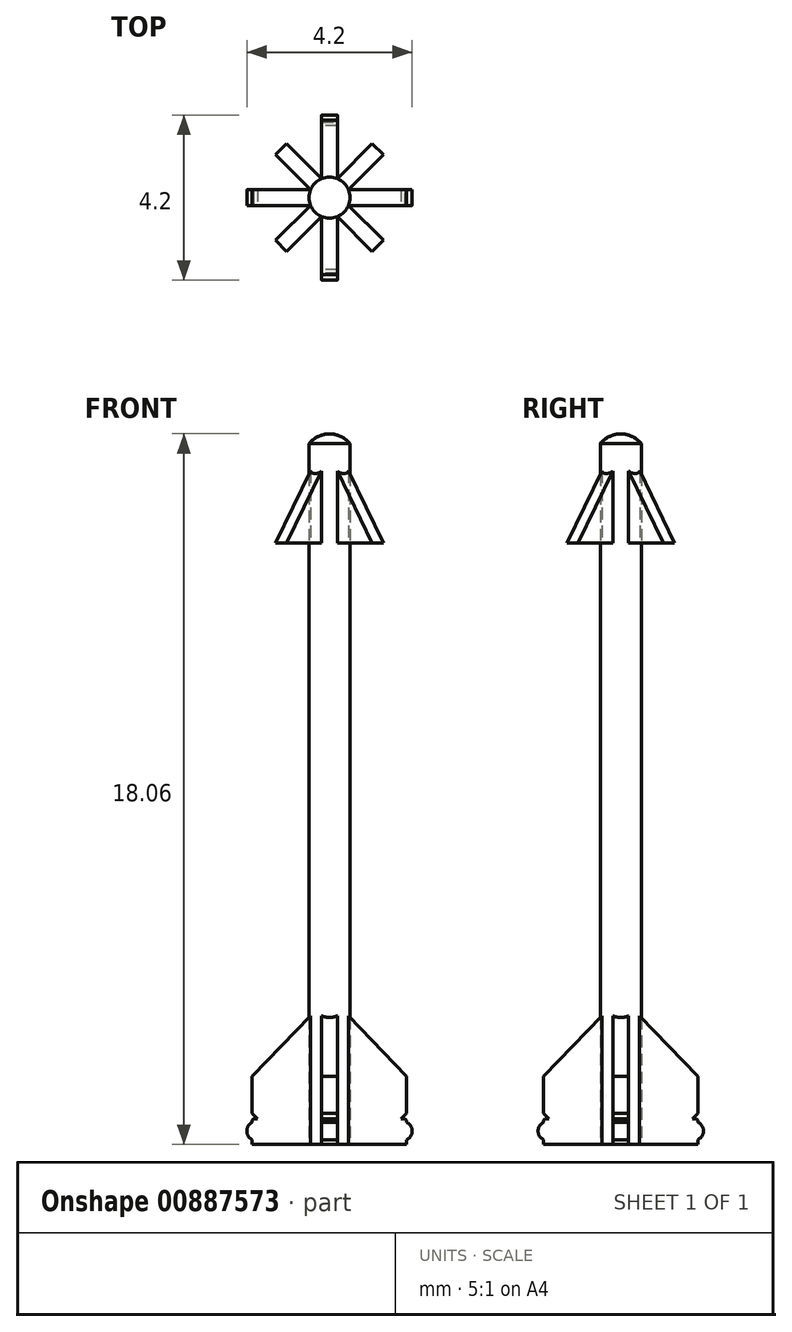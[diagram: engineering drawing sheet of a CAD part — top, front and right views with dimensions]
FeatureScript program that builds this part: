
annotation { "Feature Type Name" : "Feature", "Feature Type Description" : "" }
export const myFeature = defineFeature(function(context is Context, id is Id, definition is map)
    precondition{}
    {
        {
            var Q0;
            Q0=qCreatedBy(makeId("Front.planeOp"),FACE);
            var sketch = newSketch(context, id + "F0", { "sketchPlane" : qUnion([Q0])});
            skLineSegment(sketch, "E0", {"start": v(0, 0) * mm, "end": v(0, 18.06) * mm});
            skLineSegment(sketch, "E1", {"start": v(0.52, 17.8) * mm, "end": v(0.52, 0) * mm});
            skLineSegment(sketch, "E2", {"start": v(0.52, 0) * mm, "end": v(0, 0) * mm});
            skArc(sketch, "E3", {"start": v(0.52, 17.8) * mm, "mid": v(0.29, 17.99) * mm, "end": v(0, 18.06) * mm});
            skLineSegment(sketch, "E4", {"start": v(0, 18.06) * mm, "end": v(1.85, 18.06) * mm, "construction": true});
            skSolve(sketch);
        }
        {
            var Q0;
            Q0 = qSketchRegion(id + "F0", true);
            var Q1;
            Q1=sQuery(id+"F0.wireOp",EDGE,"E0");
            revolve(context, id + "F1", {"surfaceOperationType" : NewSurfaceOperationType.NEW, "entities" : qUnion([Q0]), "axis" : qUnion([Q1]), "revolveType" : RevolveType.FULL});
        }
        {
            var Q0;
            Q0=qCreatedBy(makeId("Front.planeOp"),FACE);
            var sketch = newSketch(context, id + "F2", { "sketchPlane" : qUnion([Q0])});
            skLineSegment(sketch, "E5", {"start": v(0.33, 3.43) * mm, "end": v(-0.33, 3.43) * mm});
            skLineSegment(sketch, "E6", {"start": v(-1.96, 1.74) * mm, "end": v(-0.33, 3.43) * mm});
            skLineSegment(sketch, "E7", {"start": v(-1.96, 1.74) * mm, "end": v(-1.96, 0.8) * mm});
            skLineSegment(sketch, "E8", {"start": v(-1.96, 0) * mm, "end": v(1.96, 0) * mm});
            skLineSegment(sketch, "E9", {"start": v(1.96, 0.8) * mm, "end": v(1.96, 1.74) * mm});
            skLineSegment(sketch, "E10", {"start": v(0.33, 3.43) * mm, "end": v(1.96, 1.74) * mm});
            skLineSegment(sketch, "E11", {"start": v(0, 0) * mm, "end": v(0, 3.43) * mm, "construction": true});
            skLineSegment(sketch, "E12", {"start": v(-0.52, 0) * mm, "end": v(-0.52, 4.16) * mm, "construction": true});
            skLineSegment(sketch, "E13.0", {"start": v(0.52, 17.8) * mm, "end": v(-0.52, 17.8) * mm});
            skPoint(sketch, "E14", {"position": v(-0.52, 3.23) * mm});
            skLineSegment(sketch, "E15", {"start": v(-1.96, 0) * mm, "end": v(-1.96, 0.12) * mm});
            skLineSegment(sketch, "E16", {"start": v(1.96, 0) * mm, "end": v(1.96, 0.12) * mm});
            skLineSegment(sketch, "E17", {"start": v(1.96, 0.8) * mm, "end": v(1.82, 0.66) * mm});
            skLineSegment(sketch, "E18", {"start": v(1.96, 0.61) * mm, "end": v(1.96, 0.56) * mm});
            skLineSegment(sketch, "E19", {"start": v(-1.96, 0.8) * mm, "end": v(-1.82, 0.66) * mm});
            skLineSegment(sketch, "E20", {"start": v(-1.96, 0.62) * mm, "end": v(-1.96, 0.56) * mm});
            skArc(sketch, "E21", {"start": v(-1.96, 0.56) * mm, "mid": v(-2.1, 0.34) * mm, "end": v(-1.96, 0.13) * mm});
            skArc(sketch, "E22", {"start": v(1.96, 0.13) * mm, "mid": v(2.1, 0.34) * mm, "end": v(1.96, 0.56) * mm});
            skLineSegment(sketch, "E23", {"start": v(-1.96, 0.62) * mm, "end": v(-1.92, 0.66) * mm});
            skLineSegment(sketch, "E24", {"start": v(-1.92, 0.66) * mm, "end": v(-1.82, 0.66) * mm});
            skLineSegment(sketch, "E25", {"start": v(1.96, 0.61) * mm, "end": v(1.93, 0.66) * mm});
            skLineSegment(sketch, "E26", {"start": v(1.93, 0.66) * mm, "end": v(1.82, 0.66) * mm});
            skSolve(sketch);
        }
        {
            var Q0;
            Q0 = qSketchRegion(id + "F2", true);
            extrude(context, id + "F3", {"entities" : qUnion([Q0]), "operationType" : NewBodyOperationType.ADD, "depth" : .4 * mm, "offsetDistance" : 25 * mm, "symmetric" : true});
        }
        {
            var Q0;
            Q0=qCreatedBy(makeId("Front.planeOp"),FACE);
            var Q1;
            Q1=qCreatedBy(makeId("Right.planeOp"),FACE);
            cPlane(context, id + "F4", {"entities" : qUnion([Q0, Q1]), "cplaneType" : CPlaneType.MID_PLANE, "offset" : 25 * mm, "width" : 150 * mm, "height" : 150 * mm});
        }
        {
            var Q0;
            Q0=qCreatedBy(id+"F4.planeOp",FACE);
            var sketch = newSketch(context, id + "F5", { "sketchPlane" : qUnion([Q0])});
            skLineSegment(sketch, "E27", {"start": v(-0.06, 17.73) * mm, "end": v(-1.74, 15.28) * mm});
            skLineSegment(sketch, "E28", {"start": v(-1.74, 15.28) * mm, "end": v(1.74, 15.28) * mm});
            skLineSegment(sketch, "E29", {"start": v(1.74, 15.28) * mm, "end": v(0.06, 17.73) * mm});
            skLineSegment(sketch, "E30", {"start": v(0.06, 17.73) * mm, "end": v(-0.06, 17.73) * mm});
            skLineSegment(sketch, "E31.0", {"start": v(0.52, 17.8) * mm, "end": v(-0.52, 17.8) * mm});
            skLineSegment(sketch, "E32", {"start": v(-0.52, 17.8) * mm, "end": v(-0.52, 15.86) * mm, "construction": true});
            skPoint(sketch, "E33", {"position": v(-0.52, 17.05) * mm});
            skLineSegment(sketch, "E34", {"start": v(0, 0) * mm, "end": v(0, 15.28) * mm, "construction": true});
            skPoint(sketch, "E34.endSnap0", {"position": v(0, 15.28) * mm});
            skSolve(sketch);
        }
        {
            var Q0;
            Q0 = qSketchRegion(id + "F5", true);
            extrude(context, id + "F6", {"entities" : qUnion([Q0]), "operationType" : NewBodyOperationType.ADD, "depth" : .4 * mm, "offsetDistance" : 25 * mm, "symmetric" : true});
        }
        {
            var Q0;
            Q0=makeQuery(id+"F1.opRevolve","SWEPT_BODY",BODY,{"disambiguationData":[OSD([sQuery(id+"F0.wireOp",EDGE,"E0"),sQuery(id+"F0.wireOp",EDGE,"E1"),sQuery(id+"F0.wireOp",EDGE,"E2"),sQuery(id+"F0.wireOp",EDGE,"E3")])]});
            var Q1;
            Q1=makeQuery(id+"F1.opRevolve","SWEPT_FACE",FACE,{"disambiguationData":[OSD([sQuery(id+"F0.wireOp",EDGE,"E1")])]});
            circularPattern(context, id + "F7", {"entities" : qUnion([Q0]), "axis" : qUnion([Q1]), "angle" : 360 * degree, "instanceCount" : 4, "equalSpace" : true, "computeTransformsWithoutBuiltin" : true});
        }
    });
